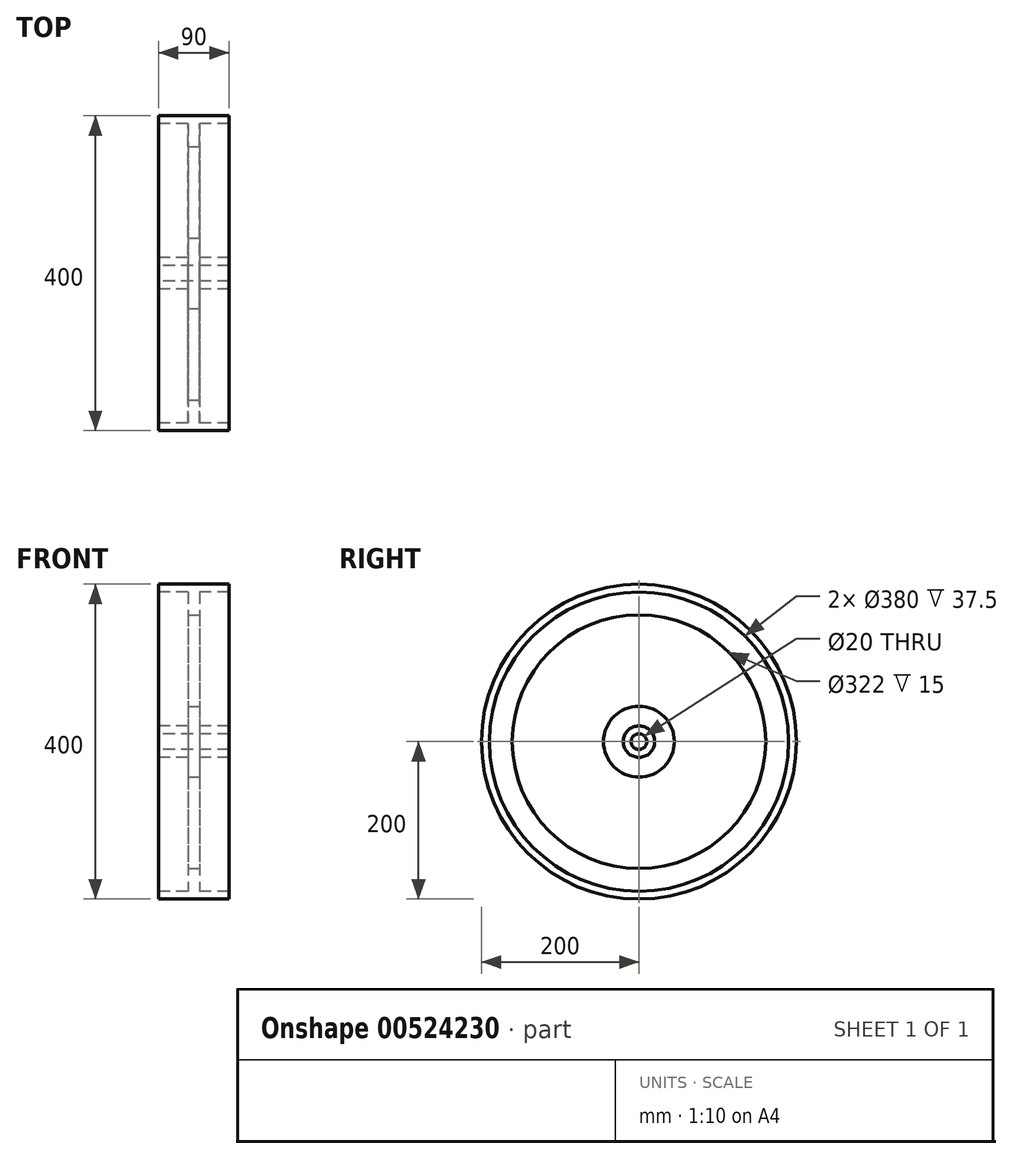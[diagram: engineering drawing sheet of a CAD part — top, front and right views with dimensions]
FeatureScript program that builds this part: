
annotation { "Feature Type Name" : "Feature", "Feature Type Description" : "" }
export const myFeature = defineFeature(function(context is Context, id is Id, definition is map)
    precondition{}
    {
        {
            var Q0;
            Q0=qCreatedBy(makeId("Top.planeOp"),FACE);
            var sketch = newSketch(context, id + "F0", { "sketchPlane" : qUnion([Q0])});
            skLineSegment(sketch, "E0", {"start": v(-75, 0) * mm, "end": v(75, 0) * mm, "construction": true});
            skLineSegment(sketch, "E1", {"start": v(0, 118.3) * mm, "end": v(0, -65.2) * mm, "construction": true});
            skLineSegment(sketch, "E2", {"start": v(-45, 10) * mm, "end": v(45, 10) * mm});
            skLineSegment(sketch, "E3", {"start": v(45, 10) * mm, "end": v(45, 20) * mm});
            skLineSegment(sketch, "E4", {"start": v(45, 20) * mm, "end": v(7.5, 20) * mm});
            skLineSegment(sketch, "E5", {"start": v(7.5, 20) * mm, "end": v(7.5, 190) * mm});
            skLineSegment(sketch, "E6", {"start": v(7.5, 190) * mm, "end": v(45, 190) * mm});
            skLineSegment(sketch, "E7", {"start": v(45, 190) * mm, "end": v(45, 200) * mm});
            skLineSegment(sketch, "E8", {"start": v(45, 200) * mm, "end": v(-45, 200) * mm});
            skLineSegment(sketch, "E9.MirrorCS", {"start": v(-45, 10) * mm, "end": v(-45, 20) * mm});
            skLineSegment(sketch, "E10.MirrorCS", {"start": v(-45, 20) * mm, "end": v(-7.5, 20) * mm});
            skLineSegment(sketch, "E11.MirrorCS", {"start": v(-7.5, 20) * mm, "end": v(-7.5, 190) * mm});
            skLineSegment(sketch, "E12.MirrorCS", {"start": v(-45, 190) * mm, "end": v(-45, 200) * mm});
            skLineSegment(sketch, "E13.MirrorCS", {"start": v(-7.5, 190) * mm, "end": v(-45, 190) * mm});
            skSolve(sketch);
        }
        {
            var Q0;
            Q0=makeQuery(id+"F0.imprint","IMPRINT",FACE,{"disambiguationData":[TD([[makeQuery(id+"F0.imprint","IMPRINT",EDGE,{"derivedFrom":sQuery(id+"F0.wireOp",EDGE,"E2")}),1.0]])]});
            var Q1;
            Q1=sQuery(id+"F0.wireOp",EDGE,"E0");
            revolve(context, id + "F1", {"entities" : qUnion([Q0]), "axis" : qUnion([Q1]), "revolveType" : RevolveType.FULL});
        }
        {
            var Q0;
            Q0=qCreatedBy(makeId("Right.planeOp"),FACE);
            var sketch = newSketch(context, id + "F2", { "sketchPlane" : qUnion([Q0])});
            skCircle(sketch, "E14.0", {"center": v(0, 0) * mm, "radius": 190 * mm});
            skCircle(sketch, "E15.0", {"center": v(0, 0) * mm, "radius": 20 * mm});
            skCircle(sketch, "E16.0", {"center": v(0, 0) * mm, "radius": 45 * mm});
            skCircle(sketch, "E17.0", {"center": v(0, 0) * mm, "radius": 161 * mm});
            skLineSegment(sketch, "E18", {"start": v(0, 0) * mm, "end": v(190, 0) * mm, "construction": true});
            skSolve(sketch);
        }
        {
            var Q0;
            Q0=makeQuery(id+"F2.imprint","IMPRINT",FACE,{"disambiguationData":[TD([[makeQuery(id+"F2.imprint","IMPRINT",EDGE,{"derivedFrom":sQuery(id+"F2.wireOp",EDGE,"E16.0")}),-1.0]])]});
            extrude(context, id + "F3", {"entities" : qUnion([Q0]), "operationType" : NewBodyOperationType.REMOVE, "endBound" : BoundingType.SYMMETRIC, "oppositeDirection" : true, "depth" : 30 * mm, "offsetDistance" : 25 * mm});
        }
    });
